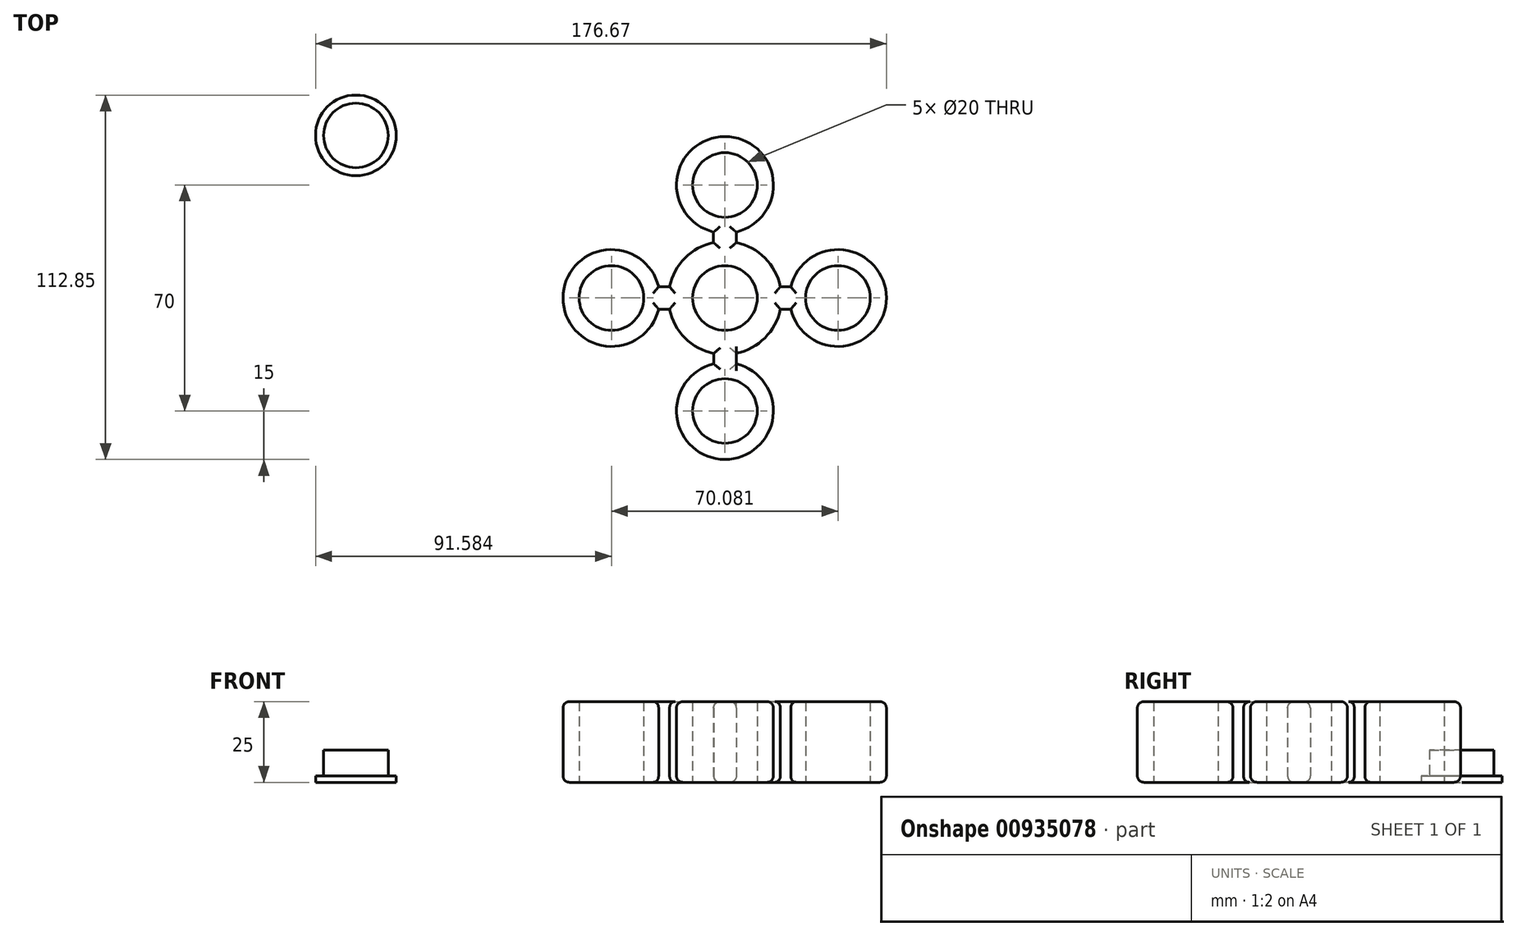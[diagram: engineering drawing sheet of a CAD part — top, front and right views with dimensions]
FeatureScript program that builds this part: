
annotation { "Feature Type Name" : "Feature", "Feature Type Description" : "" }
export const myFeature = defineFeature(function(context is Context, id is Id, definition is map)
    precondition{}
    {
        {
            var Q0;
            Q0=qCreatedBy(makeId("Top.planeOp"),FACE);
            var sketch = newSketch(context, id + "F0", { "sketchPlane" : qUnion([Q0])});
            skCircle(sketch, "E0", {"center": v(0, 0) * mm, "radius": 10 * mm});
            skCircle(sketch, "E1", {"center": v(0, 0) * mm, "radius": 17.5 * mm});
            skLineSegment(sketch, "E2.bottom", {"start": v(34.97, 3.5) * mm, "end": v(0.03, 3.5) * mm});
            skLineSegment(sketch, "E2.top", {"start": v(34.97, -3.5) * mm, "end": v(0.03, -3.5) * mm});
            skLineSegment(sketch, "E2.left", {"start": v(34.97, 3.5) * mm, "end": v(34.97, -3.5) * mm});
            skPoint(sketch, "E2.middle", {"position": v(17.5, 0) * mm});
            skLineSegment(sketch, "E3.bottom", {"start": v(0.03, 3.5) * mm, "end": v(-35.2, 3.5) * mm});
            skLineSegment(sketch, "E3.top", {"start": v(0.2, -3.5) * mm, "end": v(-35.03, -3.5) * mm});
            skLineSegment(sketch, "E3.right", {"start": v(-35.2, 3.5) * mm, "end": v(-35.03, -3.5) * mm});
            skPoint(sketch, "E3.middle", {"position": v(-17.5, 0) * mm});
            skLineSegment(sketch, "E4.bottom", {"start": v(3.53, 0) * mm, "end": v(-3.53, 0) * mm});
            skLineSegment(sketch, "E4.top", {"start": v(3.53, 35) * mm, "end": v(-3.53, 35) * mm});
            skLineSegment(sketch, "E4.left", {"start": v(3.53, 0) * mm, "end": v(3.53, 35) * mm});
            skLineSegment(sketch, "E4.right", {"start": v(-3.53, 0) * mm, "end": v(-3.53, 35) * mm});
            skPoint(sketch, "E4.middle", {"position": v(0, 17.5) * mm});
            skLineSegment(sketch, "E5.top", {"start": v(3.53, -35) * mm, "end": v(-3.47, -35) * mm});
            skLineSegment(sketch, "E5.left", {"start": v(3.53, 0) * mm, "end": v(3.53, -35) * mm});
            skLineSegment(sketch, "E5.right", {"start": v(-3.47, 0) * mm, "end": v(-3.47, -35) * mm});
            skPoint(sketch, "E5.middle", {"position": v(0.03, -17.5) * mm});
            skCircle(sketch, "E6", {"center": v(34.97, 0) * mm, "radius": 10 * mm});
            skCircle(sketch, "E7", {"center": v(34.97, 0) * mm, "radius": 15 * mm});
            skCircle(sketch, "E8", {"center": v(0, -35) * mm, "radius": 10 * mm});
            skCircle(sketch, "E9", {"center": v(0, -35) * mm, "radius": 15 * mm});
            skCircle(sketch, "E10", {"center": v(-35.12, 0) * mm, "radius": 10 * mm});
            skCircle(sketch, "E11", {"center": v(-35.12, 0) * mm, "radius": 15 * mm});
            skCircle(sketch, "E12", {"center": v(0, 35) * mm, "radius": 10 * mm});
            skCircle(sketch, "E13", {"center": v(0, 35) * mm, "radius": 15 * mm});
            skSolve(sketch);
        }
        {
            var Q0;
            {var subQ0=sQuery(id+"F0.wireOp",EDGE,"E3.top");var subQ1=sQuery(id+"F0.wireOp",EDGE,"E0");var subQ2=makeQuery(id+"F0.imprint","INTERSECT",VERTEX,{"derivedFrom":[subQ1,subQ0]});Q0=makeQuery(id+"F0.imprint","IMPRINT",FACE,{"disambiguationData":[TD([[makeQuery(id+"F0.imprint","IMPRINT",EDGE,{"disambiguationData":[TD([[subQ2,-1.0]])],"derivedFrom":subQ1}),-1.0]])]});}
            var Q1;
            {var subQ0=sQuery(id+"F0.wireOp",EDGE,"E4.right");var subQ1=sQuery(id+"F0.wireOp",EDGE,"E0");var subQ2=makeQuery(id+"F0.imprint","INTERSECT",VERTEX,{"derivedFrom":[subQ1,subQ0]});Q1=makeQuery(id+"F0.imprint","IMPRINT",FACE,{"disambiguationData":[TD([[makeQuery(id+"F0.imprint","IMPRINT",EDGE,{"disambiguationData":[TD([[subQ2,-1.0]])],"derivedFrom":subQ1}),-1.0]])]});}
            var Q2;
            {var subQ0=sQuery(id+"F0.wireOp",EDGE,"E4.left");var subQ1=sQuery(id+"F0.wireOp",EDGE,"E0");var subQ2=makeQuery(id+"F0.imprint","INTERSECT",VERTEX,{"derivedFrom":[subQ1,subQ0]});Q2=makeQuery(id+"F0.imprint","IMPRINT",FACE,{"disambiguationData":[TD([[makeQuery(id+"F0.imprint","IMPRINT",EDGE,{"disambiguationData":[TD([[subQ2,1.0]])],"derivedFrom":subQ1}),-1.0]])]});}
            var Q3;
            {var subQ0=sQuery(id+"F0.wireOp",EDGE,"E4.left");var subQ1=sQuery(id+"F0.wireOp",EDGE,"E0");var subQ2=makeQuery(id+"F0.imprint","INTERSECT",VERTEX,{"derivedFrom":[subQ1,subQ0]});Q3=makeQuery(id+"F0.imprint","IMPRINT",FACE,{"disambiguationData":[TD([[makeQuery(id+"F0.imprint","IMPRINT",EDGE,{"disambiguationData":[TD([[subQ2,-1.0]])],"derivedFrom":subQ1}),-1.0]])]});}
            var Q4;
            {var subQ0=sQuery(id+"F0.wireOp",EDGE,"E2.bottom");var subQ1=sQuery(id+"F0.wireOp",EDGE,"E0");var subQ2=makeQuery(id+"F0.imprint","INTERSECT",VERTEX,{"derivedFrom":[subQ1,subQ0]});Q4=makeQuery(id+"F0.imprint","IMPRINT",FACE,{"disambiguationData":[TD([[makeQuery(id+"F0.imprint","IMPRINT",EDGE,{"disambiguationData":[TD([[subQ2,1.0]])],"derivedFrom":subQ1}),-1.0]])]});}
            var Q5;
            {var subQ0=sQuery(id+"F0.wireOp",EDGE,"E5.left");var subQ1=sQuery(id+"F0.wireOp",EDGE,"E0");var subQ2=makeQuery(id+"F0.imprint","INTERSECT",VERTEX,{"derivedFrom":[subQ1,subQ0]});Q5=makeQuery(id+"F0.imprint","IMPRINT",FACE,{"disambiguationData":[TD([[makeQuery(id+"F0.imprint","IMPRINT",EDGE,{"disambiguationData":[TD([[subQ2,-1.0]])],"derivedFrom":subQ1}),-1.0]])]});}
            var Q6;
            {var subQ0=sQuery(id+"F0.wireOp",EDGE,"E5.right");var subQ1=sQuery(id+"F0.wireOp",EDGE,"E0");var subQ2=makeQuery(id+"F0.imprint","INTERSECT",VERTEX,{"derivedFrom":[subQ1,subQ0]});Q6=makeQuery(id+"F0.imprint","IMPRINT",FACE,{"disambiguationData":[TD([[makeQuery(id+"F0.imprint","IMPRINT",EDGE,{"disambiguationData":[TD([[subQ2,-1.0]])],"derivedFrom":subQ1}),-1.0]])]});}
            var Q7;
            {var subQ0=sQuery(id+"F0.wireOp",EDGE,"E5.right");var subQ1=sQuery(id+"F0.wireOp",EDGE,"E1");var subQ2=makeQuery(id+"F0.imprint","INTERSECT",VERTEX,{"derivedFrom":[subQ1,subQ0]});Q7=makeQuery(id+"F0.imprint","IMPRINT",FACE,{"disambiguationData":[TD([[makeQuery(id+"F0.imprint","IMPRINT",EDGE,{"disambiguationData":[TD([[subQ2,-1.0]])],"derivedFrom":subQ1}),-1.0]])]});}
            var Q8;
            {var subQ0=sQuery(id+"F0.wireOp",EDGE,"E9");var subQ1=sQuery(id+"F0.wireOp",EDGE,"E5.left");var subQ2=makeQuery(id+"F0.imprint","INTERSECT",VERTEX,{"derivedFrom":[subQ1,subQ0]});Q8=makeQuery(id+"F0.imprint","IMPRINT",FACE,{"disambiguationData":[TD([[makeQuery(id+"F0.imprint","IMPRINT",EDGE,{"disambiguationData":[TD([[subQ2,-1.0]])],"derivedFrom":subQ1}),-1.0]])]});}
            var Q9;
            {var subQ0=sQuery(id+"F0.wireOp",EDGE,"E9");var subQ1=sQuery(id+"F0.wireOp",EDGE,"E5.left");var subQ2=makeQuery(id+"F0.imprint","INTERSECT",VERTEX,{"derivedFrom":[subQ1,subQ0]});Q9=makeQuery(id+"F0.imprint","IMPRINT",FACE,{"disambiguationData":[TD([[makeQuery(id+"F0.imprint","IMPRINT",EDGE,{"disambiguationData":[TD([[subQ2,-1.0]])],"derivedFrom":subQ1}),1.0]])]});}
            var Q10;
            {var subQ0=sQuery(id+"F0.wireOp",EDGE,"E2.bottom");var subQ1=sQuery(id+"F0.wireOp",EDGE,"E1");var subQ2=makeQuery(id+"F0.imprint","INTERSECT",VERTEX,{"derivedFrom":[subQ1,subQ0]});Q10=makeQuery(id+"F0.imprint","IMPRINT",FACE,{"disambiguationData":[TD([[makeQuery(id+"F0.imprint","IMPRINT",EDGE,{"disambiguationData":[TD([[subQ2,1.0]])],"derivedFrom":subQ1}),-1.0]])]});}
            var Q11;
            {var subQ0=sQuery(id+"F0.wireOp",EDGE,"E7");var subQ1=sQuery(id+"F0.wireOp",EDGE,"E2.bottom");var subQ2=makeQuery(id+"F0.imprint","INTERSECT",VERTEX,{"derivedFrom":[subQ1,subQ0]});Q11=makeQuery(id+"F0.imprint","IMPRINT",FACE,{"disambiguationData":[TD([[makeQuery(id+"F0.imprint","IMPRINT",EDGE,{"disambiguationData":[TD([[subQ2,1.0]])],"derivedFrom":subQ1}),-1.0]])]});}
            var Q12;
            {var subQ0=sQuery(id+"F0.wireOp",EDGE,"E7");var subQ1=sQuery(id+"F0.wireOp",EDGE,"E2.bottom");var subQ2=makeQuery(id+"F0.imprint","INTERSECT",VERTEX,{"derivedFrom":[subQ1,subQ0]});Q12=makeQuery(id+"F0.imprint","IMPRINT",FACE,{"disambiguationData":[TD([[makeQuery(id+"F0.imprint","IMPRINT",EDGE,{"disambiguationData":[TD([[subQ2,1.0]])],"derivedFrom":subQ1}),1.0]])]});}
            var Q13;
            {var subQ0=sQuery(id+"F0.wireOp",EDGE,"E13");var subQ1=sQuery(id+"F0.wireOp",EDGE,"E4.left");var subQ2=makeQuery(id+"F0.imprint","INTERSECT",VERTEX,{"derivedFrom":[subQ1,subQ0]});Q13=makeQuery(id+"F0.imprint","IMPRINT",FACE,{"disambiguationData":[TD([[makeQuery(id+"F0.imprint","IMPRINT",EDGE,{"disambiguationData":[TD([[subQ2,-1.0]])],"derivedFrom":subQ1}),1.0]])]});}
            var Q14;
            {var subQ0=sQuery(id+"F0.wireOp",EDGE,"E4.left");var subQ1=sQuery(id+"F0.wireOp",EDGE,"E1");var subQ2=makeQuery(id+"F0.imprint","INTERSECT",VERTEX,{"derivedFrom":[subQ1,subQ0]});Q14=makeQuery(id+"F0.imprint","IMPRINT",FACE,{"disambiguationData":[TD([[makeQuery(id+"F0.imprint","IMPRINT",EDGE,{"disambiguationData":[TD([[subQ2,-1.0]])],"derivedFrom":subQ1}),-1.0]])]});}
            var Q15;
            {var subQ0=sQuery(id+"F0.wireOp",EDGE,"E13");var subQ1=sQuery(id+"F0.wireOp",EDGE,"E4.left");var subQ2=makeQuery(id+"F0.imprint","INTERSECT",VERTEX,{"derivedFrom":[subQ1,subQ0]});Q15=makeQuery(id+"F0.imprint","IMPRINT",FACE,{"disambiguationData":[TD([[makeQuery(id+"F0.imprint","IMPRINT",EDGE,{"disambiguationData":[TD([[subQ2,-1.0]])],"derivedFrom":subQ1}),-1.0]])]});}
            var Q16;
            {var subQ0=sQuery(id+"F0.wireOp",EDGE,"E11");var subQ1=sQuery(id+"F0.wireOp",EDGE,"E3.bottom");var subQ2=makeQuery(id+"F0.imprint","INTERSECT",VERTEX,{"derivedFrom":[subQ1,subQ0]});Q16=makeQuery(id+"F0.imprint","IMPRINT",FACE,{"disambiguationData":[TD([[makeQuery(id+"F0.imprint","IMPRINT",EDGE,{"disambiguationData":[TD([[subQ2,-1.0]])],"derivedFrom":subQ1}),1.0]])]});}
            var Q17;
            {var subQ0=sQuery(id+"F0.wireOp",EDGE,"E3.bottom");var subQ1=sQuery(id+"F0.wireOp",EDGE,"E1");var subQ2=makeQuery(id+"F0.imprint","INTERSECT",VERTEX,{"derivedFrom":[subQ1,subQ0]});Q17=makeQuery(id+"F0.imprint","IMPRINT",FACE,{"disambiguationData":[TD([[makeQuery(id+"F0.imprint","IMPRINT",EDGE,{"disambiguationData":[TD([[subQ2,-1.0]])],"derivedFrom":subQ1}),-1.0]])]});}
            var Q18;
            {var subQ0=sQuery(id+"F0.wireOp",EDGE,"E3.bottom");var subQ1=sQuery(id+"F0.wireOp",EDGE,"E0");var subQ2=makeQuery(id+"F0.imprint","INTERSECT",VERTEX,{"derivedFrom":[subQ1,subQ0]});Q18=makeQuery(id+"F0.imprint","IMPRINT",FACE,{"disambiguationData":[TD([[makeQuery(id+"F0.imprint","IMPRINT",EDGE,{"disambiguationData":[TD([[subQ2,-1.0]])],"derivedFrom":subQ1}),-1.0]])]});}
            var Q19;
            {var subQ0=sQuery(id+"F0.wireOp",EDGE,"E11");var subQ1=sQuery(id+"F0.wireOp",EDGE,"E3.bottom");var subQ2=makeQuery(id+"F0.imprint","INTERSECT",VERTEX,{"derivedFrom":[subQ1,subQ0]});Q19=makeQuery(id+"F0.imprint","IMPRINT",FACE,{"disambiguationData":[TD([[makeQuery(id+"F0.imprint","IMPRINT",EDGE,{"disambiguationData":[TD([[subQ2,-1.0]])],"derivedFrom":subQ1}),-1.0]])]});}
            extrude(context, id + "F1", {"entities" : qUnion([Q0, Q1, Q2, Q3, Q4, Q5, Q6, Q7, Q8, Q9, Q10, Q11, Q12, Q13, Q14, Q15, Q16, Q17, Q18, Q19]), "depth" : 25 * mm, "offsetDistance" : 25 * mm});
        }
        {
            var Q0;
            Q0=makeQuery(id+"F1.opExtrude","CAP_EDGE",EDGE,{"disambiguationData":[OSD([sQuery(id+"F0.wireOp",EDGE,"E7")])],"isStart":false});
            var Q1;
            Q1=makeQuery(id+"F1.opExtrude","CAP_EDGE",EDGE,{"disambiguationData":[OSD([sQuery(id+"F0.wireOp",EDGE,"E2.top")])],"isStart":false});
            var Q2;
            Q2=makeQuery(id+"F1.opExtrude","CAP_EDGE",EDGE,{"disambiguationData":[OSD([sQuery(id+"F0.wireOp",EDGE,"E2.bottom")])],"isStart":false});
            var Q3;
            {var subQ0=sQuery(id+"F0.wireOp",EDGE,"E1");Q3=makeQuery(id+"F1.opExtrude","CAP_EDGE",EDGE,{"disambiguationData":[OSD([subQ0]),TDD([makeQuery(id+"F0.imprint","IMPRINT",EDGE,{"disambiguationData":[TD([[makeQuery(id+"F0.imprint","INTERSECT",VERTEX,{"derivedFrom":[subQ0,sQuery(id+"F0.wireOp",EDGE,"E4.left")]}),1.0]])],"derivedFrom":subQ0})])],"isStart":false});}
            var Q4;
            Q4=makeQuery(id+"F1.opExtrude","CAP_EDGE",EDGE,{"disambiguationData":[OSD([sQuery(id+"F0.wireOp",EDGE,"E4.left")])],"isStart":false});
            var Q5;
            Q5=makeQuery(id+"F1.opExtrude","CAP_EDGE",EDGE,{"disambiguationData":[OSD([sQuery(id+"F0.wireOp",EDGE,"E13")])],"isStart":false});
            var Q6;
            Q6=makeQuery(id+"F1.opExtrude","CAP_EDGE",EDGE,{"disambiguationData":[OSD([sQuery(id+"F0.wireOp",EDGE,"E4.right")])],"isStart":false});
            var Q7;
            {var subQ0=sQuery(id+"F0.wireOp",EDGE,"E1");Q7=makeQuery(id+"F1.opExtrude","CAP_EDGE",EDGE,{"disambiguationData":[OSD([subQ0]),TDD([makeQuery(id+"F0.imprint","IMPRINT",EDGE,{"disambiguationData":[TD([[makeQuery(id+"F0.imprint","INTERSECT",VERTEX,{"derivedFrom":[subQ0,sQuery(id+"F0.wireOp",EDGE,"E4.right")]}),-1.0]])],"derivedFrom":subQ0})])],"isStart":false});}
            var Q8;
            Q8=makeQuery(id+"F1.opExtrude","CAP_EDGE",EDGE,{"disambiguationData":[OSD([sQuery(id+"F0.wireOp",EDGE,"E3.bottom")])],"isStart":false});
            var Q9;
            Q9=makeQuery(id+"F1.opExtrude","CAP_EDGE",EDGE,{"disambiguationData":[OSD([sQuery(id+"F0.wireOp",EDGE,"E11")])],"isStart":false});
            var Q10;
            Q10=makeQuery(id+"F1.opExtrude","CAP_EDGE",EDGE,{"disambiguationData":[OSD([sQuery(id+"F0.wireOp",EDGE,"E3.top")])],"isStart":false});
            var Q11;
            {var subQ0=sQuery(id+"F0.wireOp",EDGE,"E1");Q11=makeQuery(id+"F1.opExtrude","CAP_EDGE",EDGE,{"disambiguationData":[OSD([subQ0]),TDD([makeQuery(id+"F0.imprint","IMPRINT",EDGE,{"disambiguationData":[TD([[makeQuery(id+"F0.imprint","INTERSECT",VERTEX,{"derivedFrom":[subQ0,sQuery(id+"F0.wireOp",EDGE,"E3.top")]}),-1.0]])],"derivedFrom":subQ0})])],"isStart":false});}
            var Q12;
            Q12=makeQuery(id+"F1.opExtrude","CAP_EDGE",EDGE,{"disambiguationData":[OSD([sQuery(id+"F0.wireOp",EDGE,"E5.right")])],"isStart":false});
            var Q13;
            Q13=makeQuery(id+"F1.opExtrude","CAP_EDGE",EDGE,{"disambiguationData":[OSD([sQuery(id+"F0.wireOp",EDGE,"E9")])],"isStart":false});
            var Q14;
            {var subQ0=sQuery(id+"F0.wireOp",EDGE,"E1");Q14=makeQuery(id+"F1.opExtrude","CAP_EDGE",EDGE,{"disambiguationData":[OSD([subQ0]),TDD([makeQuery(id+"F0.imprint","IMPRINT",EDGE,{"disambiguationData":[TD([[makeQuery(id+"F0.imprint","INTERSECT",VERTEX,{"derivedFrom":[subQ0,sQuery(id+"F0.wireOp",EDGE,"E5.left")]}),-1.0]])],"derivedFrom":subQ0})])],"isStart":false});}
            fillet(context, id + "F2", {"entities" : qUnion([Q0, Q1, Q2, Q3, Q4, Q5, Q6, Q7, Q8, Q9, Q10, Q11, Q12, Q13, Q14]), "radius" : 2 * mm, "tangentPropagation" : true, "allowEdgeOverflow" : false});
        }
        {
            var Q0;
            {var subQ0=sQuery(id+"F0.wireOp",EDGE,"E1");Q0=makeQuery(id+"F1.opExtrude","CAP_EDGE",EDGE,{"disambiguationData":[OSD([subQ0]),TDD([makeQuery(id+"F0.imprint","IMPRINT",EDGE,{"disambiguationData":[TD([[makeQuery(id+"F0.imprint","INTERSECT",VERTEX,{"derivedFrom":[subQ0,sQuery(id+"F0.wireOp",EDGE,"E3.top")]}),-1.0]])],"derivedFrom":subQ0})])],"isStart":true});}
            var Q1;
            Q1=makeQuery(id+"F1.opExtrude","CAP_EDGE",EDGE,{"disambiguationData":[OSD([sQuery(id+"F0.wireOp",EDGE,"E5.right")])],"isStart":true});
            var Q2;
            Q2=makeQuery(id+"F1.opExtrude","CAP_EDGE",EDGE,{"disambiguationData":[OSD([sQuery(id+"F0.wireOp",EDGE,"E9")])],"isStart":true});
            var Q3;
            Q3=makeQuery(id+"F1.opExtrude","CAP_EDGE",EDGE,{"disambiguationData":[OSD([sQuery(id+"F0.wireOp",EDGE,"E5.left")])],"isStart":true});
            var Q4;
            {var subQ0=sQuery(id+"F0.wireOp",EDGE,"E1");Q4=makeQuery(id+"F1.opExtrude","CAP_EDGE",EDGE,{"disambiguationData":[OSD([subQ0]),TDD([makeQuery(id+"F0.imprint","IMPRINT",EDGE,{"disambiguationData":[TD([[makeQuery(id+"F0.imprint","INTERSECT",VERTEX,{"derivedFrom":[subQ0,sQuery(id+"F0.wireOp",EDGE,"E5.left")]}),-1.0]])],"derivedFrom":subQ0})])],"isStart":true});}
            var Q5;
            Q5=makeQuery(id+"F1.opExtrude","CAP_EDGE",EDGE,{"disambiguationData":[OSD([sQuery(id+"F0.wireOp",EDGE,"E2.top")])],"isStart":true});
            var Q6;
            Q6=makeQuery(id+"F1.opExtrude","CAP_EDGE",EDGE,{"disambiguationData":[OSD([sQuery(id+"F0.wireOp",EDGE,"E7")])],"isStart":true});
            var Q7;
            Q7=makeQuery(id+"F1.opExtrude","CAP_EDGE",EDGE,{"disambiguationData":[OSD([sQuery(id+"F0.wireOp",EDGE,"E2.bottom")])],"isStart":true});
            var Q8;
            {var subQ0=sQuery(id+"F0.wireOp",EDGE,"E1");Q8=makeQuery(id+"F1.opExtrude","CAP_EDGE",EDGE,{"disambiguationData":[OSD([subQ0]),TDD([makeQuery(id+"F0.imprint","IMPRINT",EDGE,{"disambiguationData":[TD([[makeQuery(id+"F0.imprint","INTERSECT",VERTEX,{"derivedFrom":[subQ0,sQuery(id+"F0.wireOp",EDGE,"E4.left")]}),1.0]])],"derivedFrom":subQ0})])],"isStart":true});}
            var Q9;
            Q9=makeQuery(id+"F1.opExtrude","CAP_EDGE",EDGE,{"disambiguationData":[OSD([sQuery(id+"F0.wireOp",EDGE,"E4.left")])],"isStart":true});
            var Q10;
            Q10=makeQuery(id+"F1.opExtrude","CAP_EDGE",EDGE,{"disambiguationData":[OSD([sQuery(id+"F0.wireOp",EDGE,"E13")])],"isStart":true});
            var Q11;
            Q11=makeQuery(id+"F1.opExtrude","CAP_EDGE",EDGE,{"disambiguationData":[OSD([sQuery(id+"F0.wireOp",EDGE,"E4.right")])],"isStart":true});
            var Q12;
            {var subQ0=sQuery(id+"F0.wireOp",EDGE,"E1");Q12=makeQuery(id+"F1.opExtrude","CAP_EDGE",EDGE,{"disambiguationData":[OSD([subQ0]),TDD([makeQuery(id+"F0.imprint","IMPRINT",EDGE,{"disambiguationData":[TD([[makeQuery(id+"F0.imprint","INTERSECT",VERTEX,{"derivedFrom":[subQ0,sQuery(id+"F0.wireOp",EDGE,"E4.right")]}),-1.0]])],"derivedFrom":subQ0})])],"isStart":true});}
            var Q13;
            Q13=makeQuery(id+"F1.opExtrude","CAP_EDGE",EDGE,{"disambiguationData":[OSD([sQuery(id+"F0.wireOp",EDGE,"E3.bottom")])],"isStart":true});
            var Q14;
            Q14=makeQuery(id+"F1.opExtrude","CAP_EDGE",EDGE,{"disambiguationData":[OSD([sQuery(id+"F0.wireOp",EDGE,"E3.top")])],"isStart":true});
            var Q15;
            Q15=makeQuery(id+"F1.opExtrude","CAP_EDGE",EDGE,{"disambiguationData":[OSD([sQuery(id+"F0.wireOp",EDGE,"E11")])],"isStart":true});
            fillet(context, id + "F3", {"entities" : qUnion([Q0, Q1, Q2, Q3, Q4, Q5, Q6, Q7, Q8, Q9, Q10, Q11, Q12, Q13, Q14, Q15]), "radius" : 2 * mm, "tangentPropagation" : true, "allowEdgeOverflow" : false});
        }
        {
            var Q0;
            Q0=qCreatedBy(makeId("Top.planeOp"),FACE);
            var sketch = newSketch(context, id + "F4", { "sketchPlane" : qUnion([Q0])});
            skCircle(sketch, "E14", {"center": v(-114.2, 50.35) * mm, "radius": 12.5 * mm});
            skCircle(sketch, "E15", {"center": v(-114.2, 50.35) * mm, "radius": 10 * mm});
            skSolve(sketch);
        }
        {
            var Q0;
            Q0=makeQuery(id+"F4.imprint","IMPRINT",FACE,{"disambiguationData":[TD([[makeQuery(id+"F4.imprint","IMPRINT",EDGE,{"derivedFrom":sQuery(id+"F4.wireOp",EDGE,"E15")}),1.0]])]});
            extrude(context, id + "F5", {"entities" : qUnion([Q0]), "depth" : 10 * mm, "offsetDistance" : 25 * mm});
        }
        {
            var Q0;
            Q0 = qSketchRegion(id + "F4", true);
            extrude(context, id + "F6", {"entities" : qUnion([Q0]), "operationType" : NewBodyOperationType.ADD, "depth" : 2 * mm, "offsetDistance" : 25 * mm});
        }
        {
            var Q0;
            Q0=makeQuery(id+"F5.opExtrude","SWEPT_BODY",BODY,{"disambiguationData":[OSD([sQuery(id+"F4.wireOp",EDGE,"E15")])]});
            transform(context, id + "F7", {"entities" : qUnion([Q0]), "transformType" : TransformType.TRANSLATION_3D, "dx" : 0 * mm, "dy" : 0 * mm, "dz" : 0 * mm, "makeCopy" : true});
        }
    });
